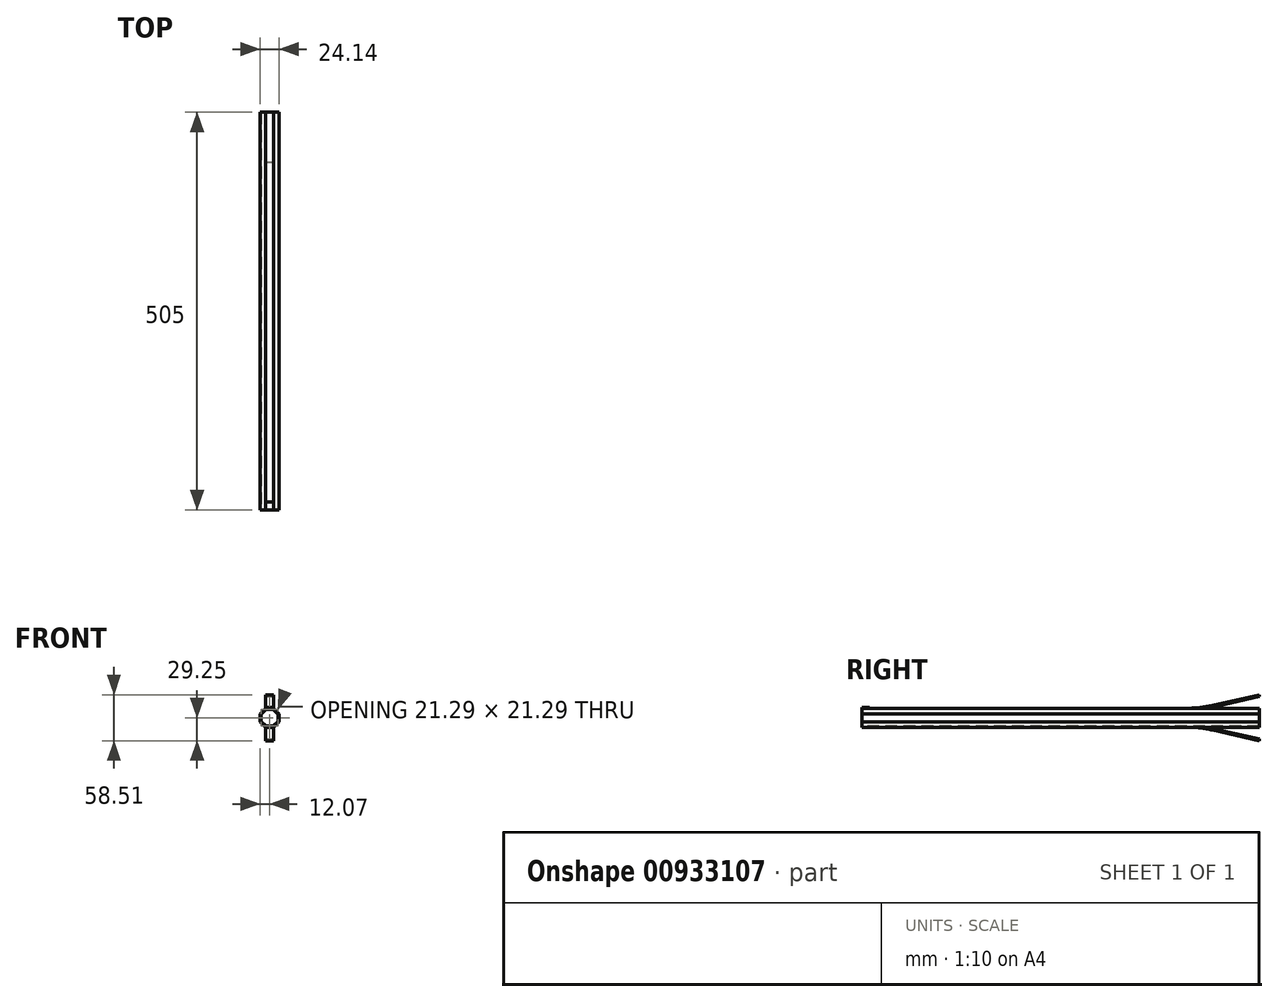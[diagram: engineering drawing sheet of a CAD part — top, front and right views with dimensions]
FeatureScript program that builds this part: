
annotation { "Feature Type Name" : "Feature", "Feature Type Description" : "" }
export const myFeature = defineFeature(function(context is Context, id is Id, definition is map)
    precondition{}
    {
        {
            var Q0;
            Q0=qCreatedBy(makeId("Front.planeOp"),FACE);
            var sketch = newSketch(context, id + "F0", { "sketchPlane" : qUnion([Q0])});
            skCircle(sketch, "E0.cCircle", {"center": v(0, 0) * mm, "radius": 12.07 * mm, "construction": true});
            skLineSegment(sketch, "E0.0", {"start": v(12.07, -5) * mm, "end": v(5, -12.07) * mm});
            skLineSegment(sketch, "E0.1", {"start": v(5, -12.07) * mm, "end": v(-5, -12.07) * mm});
            skLineSegment(sketch, "E0.2", {"start": v(-5, -12.07) * mm, "end": v(-12.07, -5) * mm});
            skLineSegment(sketch, "E0.3", {"start": v(-12.07, -5) * mm, "end": v(-12.07, 5) * mm});
            skLineSegment(sketch, "E0.4", {"start": v(-12.07, 5) * mm, "end": v(-5, 12.07) * mm});
            skLineSegment(sketch, "E0.5", {"start": v(-5, 12.07) * mm, "end": v(5, 12.07) * mm});
            skLineSegment(sketch, "E0.6", {"start": v(5, 12.07) * mm, "end": v(12.07, 5) * mm});
            skLineSegment(sketch, "E0.7", {"start": v(12.07, 5) * mm, "end": v(12.07, -5) * mm});
            skPoint(sketch, "E0.0.midPoint", {"position": v(8.54, -8.54) * mm});
            skSolve(sketch);
        }
        {
            var Q0;
            Q0 = qSketchRegion(id + "F0", true);
            extrude(context, id + "F1", {"entities" : qUnion([Q0]), "depth" : 505 * mm, "offsetDistance" : 25 * mm});
        }
        {
            var Q0;
            Q0=makeQuery(id+"F1.opExtrude","SWEPT_FACE",FACE,{"disambiguationData":[OSD([sQuery(id+"F0.wireOp",EDGE,"E0.5")])]});
            var sketch = newSketch(context, id + "F2", { "sketchPlane" : qUnion([Q0])});
            skLineSegment(sketch, "E1.bottom", {"start": v(5, -505) * mm, "end": v(-5, -505) * mm});
            skLineSegment(sketch, "E1.top", {"start": v(5, -495) * mm, "end": v(-5, -495) * mm});
            skLineSegment(sketch, "E1.left", {"start": v(5, -505) * mm, "end": v(5, -495) * mm});
            skLineSegment(sketch, "E1.right", {"start": v(-5, -505) * mm, "end": v(-5, -495) * mm});
            skPoint(sketch, "E1.middle", {"position": v(0, -500) * mm});
            skSolve(sketch);
        }
        {
            var Q0;
            Q0=makeQuery(id+"F1.opExtrude","CAP_FACE",FACE,{"disambiguationData":[OSD([sQuery(id+"F0.wireOp",EDGE,"E0.0"),sQuery(id+"F0.wireOp",EDGE,"E0.1"),sQuery(id+"F0.wireOp",EDGE,"E0.2"),sQuery(id+"F0.wireOp",EDGE,"E0.3"),sQuery(id+"F0.wireOp",EDGE,"E0.4"),sQuery(id+"F0.wireOp",EDGE,"E0.5"),sQuery(id+"F0.wireOp",EDGE,"E0.6"),sQuery(id+"F0.wireOp",EDGE,"E0.7")])],"isStart":false});
            var sketch = newSketch(context, id + "F3", { "sketchPlane" : qUnion([Q0])});
            skCircle(sketch, "E2.cCircle", {"center": v(0, 0) * mm, "radius": 10.65 * mm, "construction": true});
            skLineSegment(sketch, "E2.0", {"start": v(4.4, -10.65) * mm, "end": v(-4.4, -10.65) * mm});
            skLineSegment(sketch, "E2.1", {"start": v(-4.4, -10.65) * mm, "end": v(-10.65, -4.4) * mm});
            skLineSegment(sketch, "E2.2", {"start": v(-10.65, -4.4) * mm, "end": v(-10.65, 4.4) * mm});
            skLineSegment(sketch, "E2.3", {"start": v(-10.65, 4.4) * mm, "end": v(-4.4, 10.65) * mm});
            skLineSegment(sketch, "E2.4", {"start": v(-4.4, 10.65) * mm, "end": v(4.4, 10.65) * mm});
            skLineSegment(sketch, "E2.5", {"start": v(4.4, 10.65) * mm, "end": v(10.65, 4.4) * mm});
            skLineSegment(sketch, "E2.6", {"start": v(10.65, 4.4) * mm, "end": v(10.65, -4.4) * mm});
            skLineSegment(sketch, "E2.7", {"start": v(10.65, -4.4) * mm, "end": v(4.4, -10.65) * mm});
            skPoint(sketch, "E2.0.midPoint", {"position": v(0, -10.65) * mm});
            skSolve(sketch);
        }
        {
            var Q0;
            Q0=makeQuery(id+"F3.imprint","IMPRINT",FACE,{"disambiguationData":[TD([[makeQuery(id+"F3.imprint","IMPRINT",EDGE,{"derivedFrom":sQuery(id+"F3.wireOp",EDGE,"E2.0")}),-1.0]])]});
            extrude(context, id + "F4", {"entities" : qUnion([Q0]), "operationType" : NewBodyOperationType.REMOVE, "oppositeDirection" : true, "depth" : 505 * mm, "offsetDistance" : 25 * mm});
        }
        {
            var Q0;
            Q0=makeQuery(id+"F2.imprint","IMPRINT",FACE,{"disambiguationData":[TD([[makeQuery(id+"F2.imprint","IMPRINT",EDGE,{"derivedFrom":sQuery(id+"F2.wireOp",EDGE,"E1.bottom")}),1.0]])]});
            extrude(context, id + "F5", {"entities" : qUnion([Q0]), "operationType" : NewBodyOperationType.ADD, "depth" : 1 * mm, "offsetDistance" : 25 * mm});
        }
        {
            var Q0;
            Q0=makeQuery(id+"F1.opExtrude","SWEPT_FACE",FACE,{"disambiguationData":[OSD([sQuery(id+"F0.wireOp",EDGE,"E0.1")])]});
            var sketch = newSketch(context, id + "F6", { "sketchPlane" : qUnion([Q0])});
            skLineSegment(sketch, "E3.bottom", {"start": v(-5, 0) * mm, "end": v(5, 0) * mm});
            skLineSegment(sketch, "E3.top", {"start": v(-5, 74.89) * mm, "end": v(5, 74.89) * mm});
            skLineSegment(sketch, "E3.left", {"start": v(-5, 0) * mm, "end": v(-5, 74.89) * mm});
            skLineSegment(sketch, "E3.right", {"start": v(5, 0) * mm, "end": v(5, 74.89) * mm});
            skPoint(sketch, "E3.middle", {"position": v(0, 37.44) * mm});
            skSolve(sketch);
        }
        {
            var Q0;
            Q0=makeQuery(id+"F6.imprint","IMPRINT",FACE,{"disambiguationData":[TD([[makeQuery(id+"F6.imprint","IMPRINT",EDGE,{"derivedFrom":sQuery(id+"F6.wireOp",EDGE,"E3.bottom")}),-1.0]])]});
            extrude(context, id + "F7", {"entities" : qUnion([Q0]), "operationType" : NewBodyOperationType.ADD, "depth" : 100 * mm, "offsetDistance" : 25 * mm});
        }
        {
            var Q0;
            Q0=makeQuery(id+"F7.opExtrude","SWEPT_FACE",FACE,{"disambiguationData":[OSD([sQuery(id+"F6.wireOp",EDGE,"E3.right")])]});
            var sketch = newSketch(context, id + "F8", { "sketchPlane" : qUnion([Q0])});
            skLineSegment(sketch, "E4", {"start": v(-74.89, -12.07) * mm, "end": v(0, -29.25) * mm});
            skLineSegment(sketch, "E5", {"start": v(0, -29.25) * mm, "end": v(10.8, -84.25) * mm});
            skLineSegment(sketch, "E6", {"start": v(10.8, -84.25) * mm, "end": v(10.8, -134.84) * mm});
            skLineSegment(sketch, "E7", {"start": v(10.8, -134.84) * mm, "end": v(-107.8, -121.72) * mm});
            skLineSegment(sketch, "E8", {"start": v(-107.8, -121.72) * mm, "end": v(-74.89, -12.07) * mm});
            skSolve(sketch);
        }
        {
            var Q0;
            Q0 = qSketchRegion(id + "F8", true);
            extrude(context, id + "F9", {"entities" : qUnion([Q0]), "operationType" : NewBodyOperationType.REMOVE, "oppositeDirection" : true, "depth" : 100 * mm, "offsetDistance" : 25 * mm});
        }
        {
            var Q0;
            Q0=makeQuery(id+"F7.opExtrude","SWEPT_FACE",FACE,{"disambiguationData":[OSD([sQuery(id+"F6.wireOp",EDGE,"E3.right")])]});
            var sketch = newSketch(context, id + "F10", { "sketchPlane" : qUnion([Q0])});
            skLineSegment(sketch, "E9", {"start": v(-65.8, -12.07) * mm, "end": v(0, -27.17) * mm});
            skLineSegment(sketch, "E10", {"start": v(0, -27.17) * mm, "end": v(0, -12.07) * mm});
            skLineSegment(sketch, "E11", {"start": v(0, -12.07) * mm, "end": v(-65.8, -12.07) * mm});
            skSolve(sketch);
        }
        {
            var Q0;
            Q0=makeQuery(id+"F10.imprint","IMPRINT",FACE,{"disambiguationData":[TD([[makeQuery(id+"F10.imprint","IMPRINT",EDGE,{"derivedFrom":sQuery(id+"F10.wireOp",EDGE,"E9")}),1.0]])]});
            extrude(context, id + "F11", {"entities" : qUnion([Q0]), "operationType" : NewBodyOperationType.REMOVE, "oppositeDirection" : true, "depth" : 100 * mm, "offsetDistance" : 25 * mm});
        }
        {
            var Q0;
            {var subQ0=sQuery(id+"F6.wireOp",EDGE,"E3.top");Q0=makeQuery(id+"F9.boolean.opBoolean","MERGE",EDGE,{"derivedFrom":[makeQuery(id+"F7.opExtrude","CAP_EDGE",EDGE,{"disambiguationData":[OSD([subQ0])],"isStart":true})],"fromTools":[makeQuery(id+"F9.opExtrude","SWEPT_EDGE",EDGE,{"disambiguationData":[OSD([sQuery(id+"F0.wireOp",EDGE,"E0.0"),sQuery(id+"F0.wireOp",EDGE,"E0.1"),subQ0,sQuery(id+"F6.wireOp",EDGE,"E3.right"),sQuery(id+"F8.wireOp",EDGE,"E4"),sQuery(id+"F8.wireOp",EDGE,"E8")])]})]});}
            fillet(context, id + "F12", {"entities" : qUnion([Q0]), "radius" : 140.82 * mm, "tangentPropagation" : true, "allowEdgeOverflow" : false});
        }
        {
            var Q0;
            Q0=makeQuery(id+"F11.boolean.opBoolean","COPY",EDGE,{"derivedFrom":makeQuery(id+"F11.opExtrude","SWEPT_EDGE",EDGE,{"disambiguationData":[OSD([sQuery(id+"F0.wireOp",EDGE,"E0.0"),sQuery(id+"F0.wireOp",EDGE,"E0.1"),sQuery(id+"F6.wireOp",EDGE,"E3.right"),sQuery(id+"F10.wireOp",EDGE,"E9"),sQuery(id+"F10.wireOp",EDGE,"E11")])]})});
            fillet(context, id + "F13", {"entities" : qUnion([Q0]), "radius" : 0.3 * mm, "tangentPropagation" : true, "allowEdgeOverflow" : false});
        }
        {
            var Q0;
            Q0=makeQuery(id+"F1.opExtrude","SWEPT_FACE",FACE,{"disambiguationData":[OSD([sQuery(id+"F0.wireOp",EDGE,"E0.5")])]});
            var sketch = newSketch(context, id + "F14", { "sketchPlane" : qUnion([Q0])});
            skLineSegment(sketch, "E12.bottom", {"start": v(-5, -74.89) * mm, "end": v(5, -74.89) * mm});
            skLineSegment(sketch, "E12.top", {"start": v(-5, 0) * mm, "end": v(5, 0) * mm});
            skLineSegment(sketch, "E12.left", {"start": v(-5, -74.89) * mm, "end": v(-5, 0) * mm});
            skLineSegment(sketch, "E12.right", {"start": v(5, -74.89) * mm, "end": v(5, 0) * mm});
            skSolve(sketch);
        }
        {
            var Q0;
            Q0=makeQuery(id+"F14.imprint","IMPRINT",FACE,{"disambiguationData":[TD([[makeQuery(id+"F14.imprint","IMPRINT",EDGE,{"derivedFrom":sQuery(id+"F14.wireOp",EDGE,"E12.bottom")}),1.0]])]});
            extrude(context, id + "F15", {"entities" : qUnion([Q0]), "operationType" : NewBodyOperationType.ADD, "depth" : 100 * mm, "offsetDistance" : 25 * mm});
        }
        {
            var Q0;
            Q0=makeQuery(id+"F15.opExtrude","SWEPT_FACE",FACE,{"disambiguationData":[OSD([sQuery(id+"F14.wireOp",EDGE,"E12.right")])]});
            var sketch = newSketch(context, id + "F16", { "sketchPlane" : qUnion([Q0])});
            skLineSegment(sketch, "E13", {"start": v(-74.89, 12.07) * mm, "end": v(0, 29.26) * mm});
            skSolve(sketch);
        }
        {
            var Q0;
            Q0 = qSketchRegion(id + "F16", true);
            var Q1;
            {var subQ0=sQuery(id+"F16.wireOp",EDGE,"E13");Q1=makeQuery(id+"F16.imprint","IMPRINT",FACE,{"disambiguationData":[TD([[makeQuery(id+"F16.imprint","IMPRINT",EDGE,{"derivedFrom":subQ0}),1.0]])]});}
            extrude(context, id + "F17", {"entities" : qUnion([Q0, Q1]), "operationType" : NewBodyOperationType.REMOVE, "oppositeDirection" : true, "depth" : 25 * mm, "offsetDistance" : 25 * mm});
        }
        {
            var Q0;
            Q0=makeQuery(id+"F15.opExtrude","SWEPT_FACE",FACE,{"disambiguationData":[OSD([sQuery(id+"F14.wireOp",EDGE,"E12.right")])]});
            var sketch = newSketch(context, id + "F18", { "sketchPlane" : qUnion([Q0])});
            skLineSegment(sketch, "E14", {"start": v(-65.46, 12.07) * mm, "end": v(0, 27.1) * mm});
            skLineSegment(sketch, "E15", {"start": v(0, 27.1) * mm, "end": v(0, 12.07) * mm});
            skLineSegment(sketch, "E16", {"start": v(0, 12.07) * mm, "end": v(-65.46, 12.07) * mm});
            skSolve(sketch);
        }
        {
            var Q0;
            Q0=makeQuery(id+"F18.imprint","IMPRINT",FACE,{"disambiguationData":[TD([[makeQuery(id+"F18.imprint","IMPRINT",EDGE,{"derivedFrom":sQuery(id+"F18.wireOp",EDGE,"E14")}),-1.0]])]});
            extrude(context, id + "F19", {"entities" : qUnion([Q0]), "operationType" : NewBodyOperationType.REMOVE, "oppositeDirection" : true, "depth" : 25 * mm, "offsetDistance" : 25 * mm});
        }
        {
            var Q0;
            Q0=makeQuery(id+"F19.boolean.opBoolean","COPY",EDGE,{"derivedFrom":makeQuery(id+"F19.opExtrude","SWEPT_EDGE",EDGE,{"disambiguationData":[OSD([sQuery(id+"F0.wireOp",EDGE,"E0.5"),sQuery(id+"F0.wireOp",EDGE,"E0.6"),sQuery(id+"F14.wireOp",EDGE,"E12.right"),sQuery(id+"F18.wireOp",EDGE,"E14"),sQuery(id+"F18.wireOp",EDGE,"E16")])]})});
            fillet(context, id + "F20", {"entities" : qUnion([Q0]), "radius" : 0.3 * mm, "tangentPropagation" : true, "allowEdgeOverflow" : false});
        }
        {
            var Q0;
            {var subQ0=sQuery(id+"F14.wireOp",EDGE,"E12.bottom");Q0=makeQuery(id+"F17.boolean.opBoolean","MERGE",EDGE,{"derivedFrom":[makeQuery(id+"F15.opExtrude","CAP_EDGE",EDGE,{"disambiguationData":[OSD([subQ0])],"isStart":true})],"fromTools":[makeQuery(id+"F17.opExtrude","SWEPT_EDGE",EDGE,{"disambiguationData":[OSD([sQuery(id+"F0.wireOp",EDGE,"E0.5"),sQuery(id+"F0.wireOp",EDGE,"E0.6"),subQ0,sQuery(id+"F14.wireOp",EDGE,"E12.right"),sQuery(id+"F16.wireOp",EDGE,"E13")])]})]});}
            fillet(context, id + "F21", {"entities" : qUnion([Q0]), "radius" : 140.88 * mm, "tangentPropagation" : true, "allowEdgeOverflow" : false});
        }
    });
